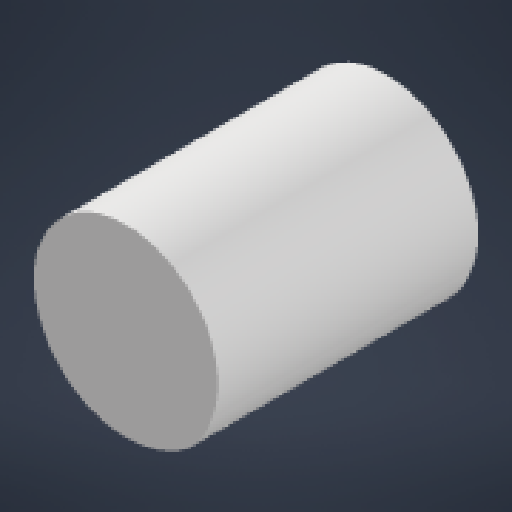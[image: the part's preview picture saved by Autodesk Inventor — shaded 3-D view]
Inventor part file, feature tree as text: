
AUTODESK INVENTOR PART (.ipt)
format: ipt  version: 2024 (Build 280153000, 153)  size: 107,008 bytes
history: native  units: in
note: dims shown in document units (in); Inventor stores cm internally (conversion verified against a paired STEP export)
features: other x3, extrude x1, sketch x1, reference x1
ambient origin geometry x8: Origin, YZ Plane, XZ Plane, XY Plane, X Axis, Y Axis, Z Axis, Center Point
bodies: Solid1 (feature_tree)
feature tree (6):
  extrude  "Extrusion1"  [1 undecoded]
  sketch  "Sketch1"  dims[d0=1.0in d1=0.0in]
  reference  "Reference1"
  other  "<userpath>\Desktop\Camera_Mount.iam"
  other  "Camera_Mount.iam"
  other  "Neck_Cover:1"
note: 1 required parameter value undecoded (feature->parameter linkage not recoverable at this tier; creation-order binding heuristic only, values carry confidence <= 0.55)
